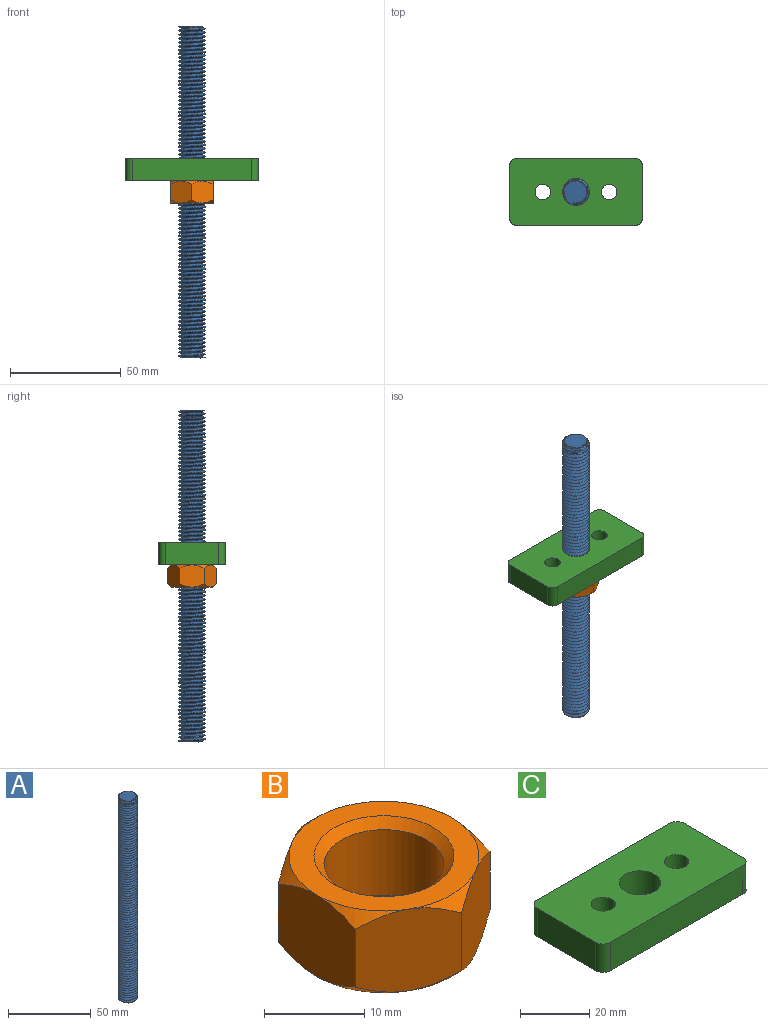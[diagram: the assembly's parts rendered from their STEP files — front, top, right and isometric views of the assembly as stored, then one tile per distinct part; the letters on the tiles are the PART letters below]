
ASSEMBLY  parts=3 mates=2
PART A: 7 faces, bbox 12.9x14.7x152.8 mm
  f0: plane 1.08x0.87mm, normal (0,-1,0), area 0.5mm2, adj f2,f4,f6
  f1: bspline ~151.08x13.86mm, area 4068mm2, adj f2,f4,f5,f6
  f2: cylinder r=4.92mm len=150mm, axis (0,0,-1), area -4.4mm2, adj f0,f1,f3,f4,f5,f6
  f3: plane 11.65x11.26mm, normal (0,0,1), area 85.1mm2, adj f2,f5,f6
  f4: plane 11.8x11.27mm, normal (0,0,-1), area 85.1mm2, adj f0,f1,f2
  f5: plane 1.05x0.87mm, normal (0.97,-0.22,0), area 0.5mm2, adj f1,f2,f3
  f6: bspline ~151.08x13.86mm, area 4050mm2, adj f0,f1,f2,f3
PART B: 23 faces, bbox 21.9x21.9x10 mm
  f0: plane 19x19mm, normal (0,0,1), area 129.6mm2, adj f5,f6,f8,f10,f12,f14,f22
  f1: plane 19x19mm, normal (0,0,-1), area 129.6mm2, adj f3,f4,f7,f9,f11,f13,f21
  f2: cylinder r=6mm len=12mm, axis (0,0,-1), area 301.6mm2, adj f21,f22
  f3: cone r=11mm half-angle=45deg, axis (0,0,1), area 6.9mm2, adj f1,f15,f16
  f4: cone r=11mm half-angle=45deg, axis (0,0,1), area 6.9mm2, adj f1,f15,f20
  f5: cone r=11mm half-angle=45deg, axis (0,0,-1), area 6.9mm2, adj f0,f15,f16
  f6: cone r=11mm half-angle=45deg, axis (0,0,-1), area 6.9mm2, adj f0,f15,f20
  f7: cone r=11mm half-angle=45deg, axis (0,0,1), area 6.9mm2, adj f1,f16,f17
  f8: cone r=11mm half-angle=45deg, axis (0,0,-1), area 6.9mm2, adj f0,f16,f17
  f9: cone r=11mm half-angle=45deg, axis (0,0,1), area 6.9mm2, adj f1,f17,f18
  f10: cone r=11mm half-angle=45deg, axis (0,0,-1), area 6.9mm2, adj f0,f17,f18
  f11: cone r=11mm half-angle=45deg, axis (0,0,1), area 6.9mm2, adj f1,f18,f19
  f12: cone r=11mm half-angle=45deg, axis (0,0,-1), area 6.9mm2, adj f0,f18,f19
  f13: cone r=11mm half-angle=45deg, axis (0,0,1), area 6.9mm2, adj f1,f19,f20
  f14: cone r=11mm half-angle=45deg, axis (0,0,-1), area 6.9mm2, adj f0,f19,f20
  f15: plane 10.01x9.5mm, normal (0.5,0.87,0), area 98.6mm2, adj f3,f4,f5,f6,f16,f20
  f16: plane 10.99x10.02mm, normal (1,0,0), area 98.6mm2, adj f3,f5,f7,f8,f15,f17
  f17: plane 10.01x9.5mm, normal (0.5,-0.87,0), area 98.6mm2, adj f7,f8,f9,f10,f16,f18
  f18: plane 10.01x9.5mm, normal (-0.5,-0.87,0), area 98.6mm2, adj f9,f10,f11,f12,f17,f19
  f19: plane 10.99x10.02mm, normal (-1,0,0), area 98.6mm2, adj f11,f12,f13,f14,f18,f20
  f20: plane 10.01x9.5mm, normal (-0.5,0.87,0), area 98.6mm2, adj f4,f6,f13,f14,f15,f19
  f21: cone r=7mm half-angle=45deg, axis (0,0,-1), area 57.8mm2, adj f1,f2
  f22: cone r=6mm half-angle=45deg, axis (0,0,1), area 57.8mm2, adj f0,f2
PART C: 15 faces, bbox 60x30x10 mm
  f0: plane 54x10mm, normal (0,1,0), area 540mm2, adj f7,f8,f11,f14
  f1: plane 24x10mm, normal (-1,0,0), area 240mm2, adj f7,f8,f11,f12
  f2: plane 54x10mm, normal (0,-1,0), area 540mm2, adj f7,f8,f12,f13
  f3: cylinder r=6mm len=12mm, axis (0,0,-1), area 377mm2, adj f7,f8
  f4: cylinder r=3.5mm len=7mm, axis (0,0,-1), area 153.9mm2, adj f7,f10
  f5: cylinder r=3.5mm len=7mm, axis (0,0,-1), area 153.9mm2, adj f7,f9
  f6: plane 24x10mm, normal (1,0,0), area 240mm2, adj f7,f8,f13,f14
  f7: plane 60x30mm, normal (0,0,1), area 1602.2mm2, adj f0,f1,f2,f3,f4,f5,f6,f11
  f8: plane 60x30mm, normal (0,0,-1), area 1413.7mm2, adj f0,f1,f2,f3,f6,f9,f10,f11
  f9: cone r=3.5mm half-angle=45deg, axis (0,0,-1), area 133.3mm2, adj f5,f8
  f10: cone r=6.5mm half-angle=45deg, axis (0,0,-1), area 133.3mm2, adj f4,f8
  f11: cylinder r=3mm len=10mm, axis (0,0,1), area 47.1mm2, adj f0,f1,f7,f8
  f12: cylinder r=3mm len=10mm, axis (0,0,-1), area 47.1mm2, adj f1,f2,f7,f8
  f13: cylinder r=3mm len=10mm, axis (0,0,1), area 47.1mm2, adj f2,f6,f7,f8
  f14: cylinder r=3mm len=10mm, axis (0,0,-1), area 47.1mm2, adj f0,f6,f7,f8
PLACE A t=(-57.3,4.39,24.75)mm
PLACE B t=(-57.3,4.39,94.75)mm
PLACE C t=(-57.3,4.39,104.75)mm
MATE fastened B.f3 <-> A.f2  axis (0,0,-1) through (-57.3,4.39,94.75)mm
MATE fastened C.f3 <-> B.f3  axis (0,0,-1) through (-57.3,4.39,104.75)mm
